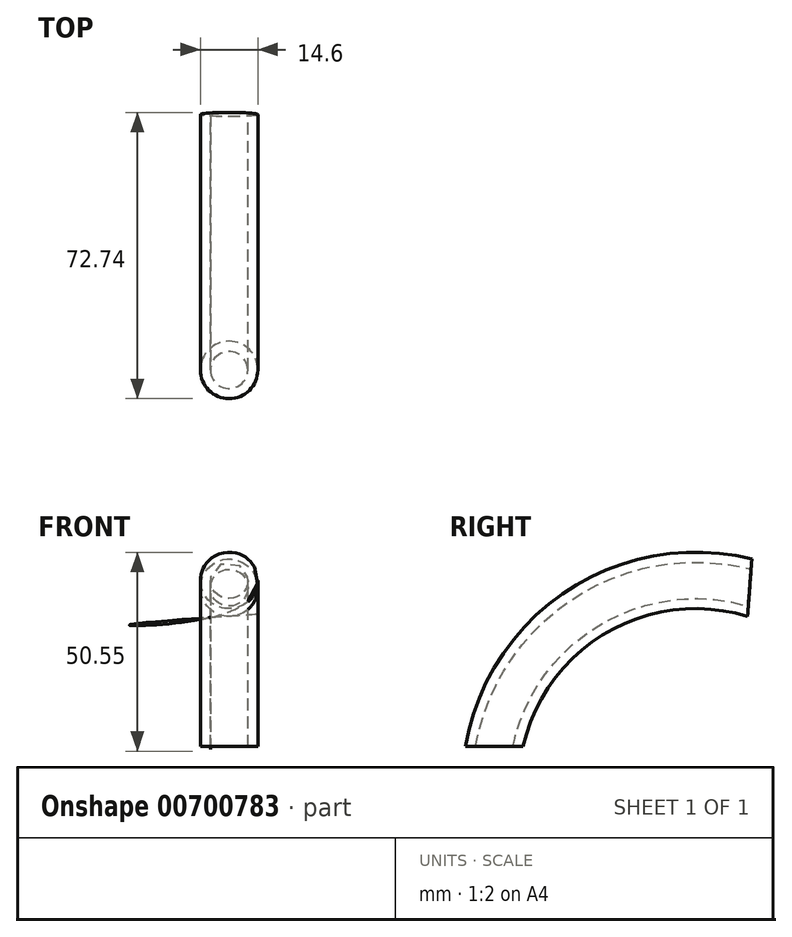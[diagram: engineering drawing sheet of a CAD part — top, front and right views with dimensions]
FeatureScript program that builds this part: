
annotation { "Feature Type Name" : "Feature", "Feature Type Description" : "" }
export const myFeature = defineFeature(function(context is Context, id is Id, definition is map)
    precondition{}
    {
        {
            var Q0;
            Q0=qCreatedBy(makeId("Right.planeOp"),FACE);
            var sketch = newSketch(context, id + "F0", { "sketchPlane" : qUnion([Q0])});
            skArc(sketch, "E0", {"start": v(-35.24, 40.35) * mm, "mid": v(-76.49, 34.34) * mm, "end": v(-100.13, 0) * mm});
            skSolve(sketch);
        }
        {
            var Q0;
            Q0=qCreatedBy(makeId("Top.planeOp"),FACE);
            var sketch = newSketch(context, id + "F1", { "sketchPlane" : qUnion([Q0])});
            skCircle(sketch, "E1", {"center": v(0, -100.13) * mm, "radius": 7.3 * mm});
            skSolve(sketch);
        }
        {
            var Q0;
            Q0 = qSketchRegion(id + "F1", true);
            var Q1;
            Q1 = qConstructionFilter(qBodyType(qCreatedBy(id + "F0" ,EDGE), BodyType.WIRE), ConstructionObject.NO);
            sweep(context, id + "F2", {"profiles" : qUnion([Q0]), "path" : qUnion([Q1])});
        }
        {
            var Q0;
            Q0=makeQuery(id+"F2.opSweep","CAP_FACE",FACE,{"disambiguationData":[OSD([sQuery(id+"F0.wireOp",VERTEX,"E0.end"),sQuery(id+"F1.wireOp",EDGE,"E1")])],"isStart":true});
            var Q1;
            Q1=makeQuery(id+"F2.opSweep","CAP_FACE",FACE,{"disambiguationData":[OSD([sQuery(id+"F0.wireOp",VERTEX,"E0.start"),sQuery(id+"F1.wireOp",EDGE,"E1")])],"isStart":false});
            shell(context, id + "F3", {"entities" : qUnion([Q0, Q1]), "thickness" : 2.54 * mm});
        }
    });
